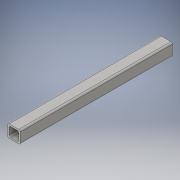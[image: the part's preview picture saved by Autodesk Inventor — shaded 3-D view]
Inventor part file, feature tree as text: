
AUTODESK INVENTOR PART (.ipt)
format: ipt  version: 2016 (Build 200138000, 138)  size: 112,640 bytes
history: native  units: in
note: dims shown in document units (in); Inventor stores cm internally (conversion verified against a paired STEP export)
features: extrude x1, sketch x1
ambient origin geometry x8: Origin, YZ Plane, XZ Plane, XY Plane, X Axis, Y Axis, Z Axis, Center Point
bodies: Solid1 (feature_tree)
feature tree (2):
  extrude  "Extrusion1"  Depth=1.0in
  sketch  "Sketch1"  dims[d0=1.0in d1=1.0in d2=0.125in d3=0.125in d4=12.0in d5=0.0in]
